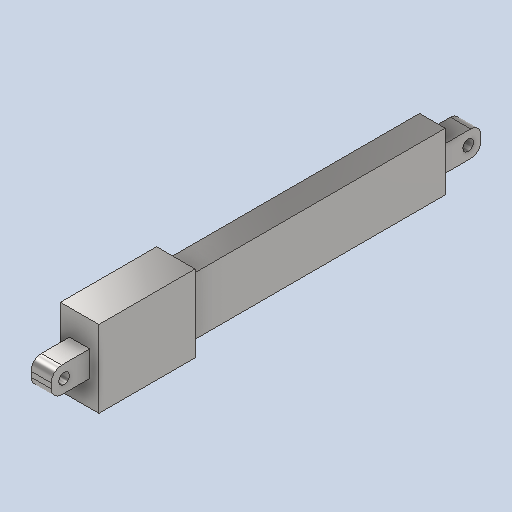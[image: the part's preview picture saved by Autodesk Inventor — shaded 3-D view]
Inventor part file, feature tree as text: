
AUTODESK INVENTOR PART (.ipt)
format: ipt  version: 2024 (Build 280153000, 153)  size: 292,864 bytes
history: native  units: mm
features: extrude x5, sketch x5, other x2, mirror x2, fillet x1
ambient origin geometry x8: Origin, YZ Plane, XZ Plane, XY Plane, X Axis, Y Axis, Z Axis, Center Point
bodies: Body1 (feature_tree)
feature tree (15):
  other  "솔리드1"
  extrude  "돌출1"  Depth=15.0mm
  extrude  "돌출2"  Depth=30.0mm
  extrude  "돌출3"  Depth=15.0mm
  extrude  "돌출4"  Depth=7.5mm
  extrude  "돌출5"  Depth=37.5mm TaperAngle=0.0deg
  other  "작업 평면1"
  mirror  "미러1"
  mirror  "미러2"
  fillet  "모깎기1"  Radius=10.0mm
  sketch  "스케치1"
  sketch  "스케치2"
  sketch  "스케치3"
  sketch  "스케치4"
  sketch  "스케치5"
